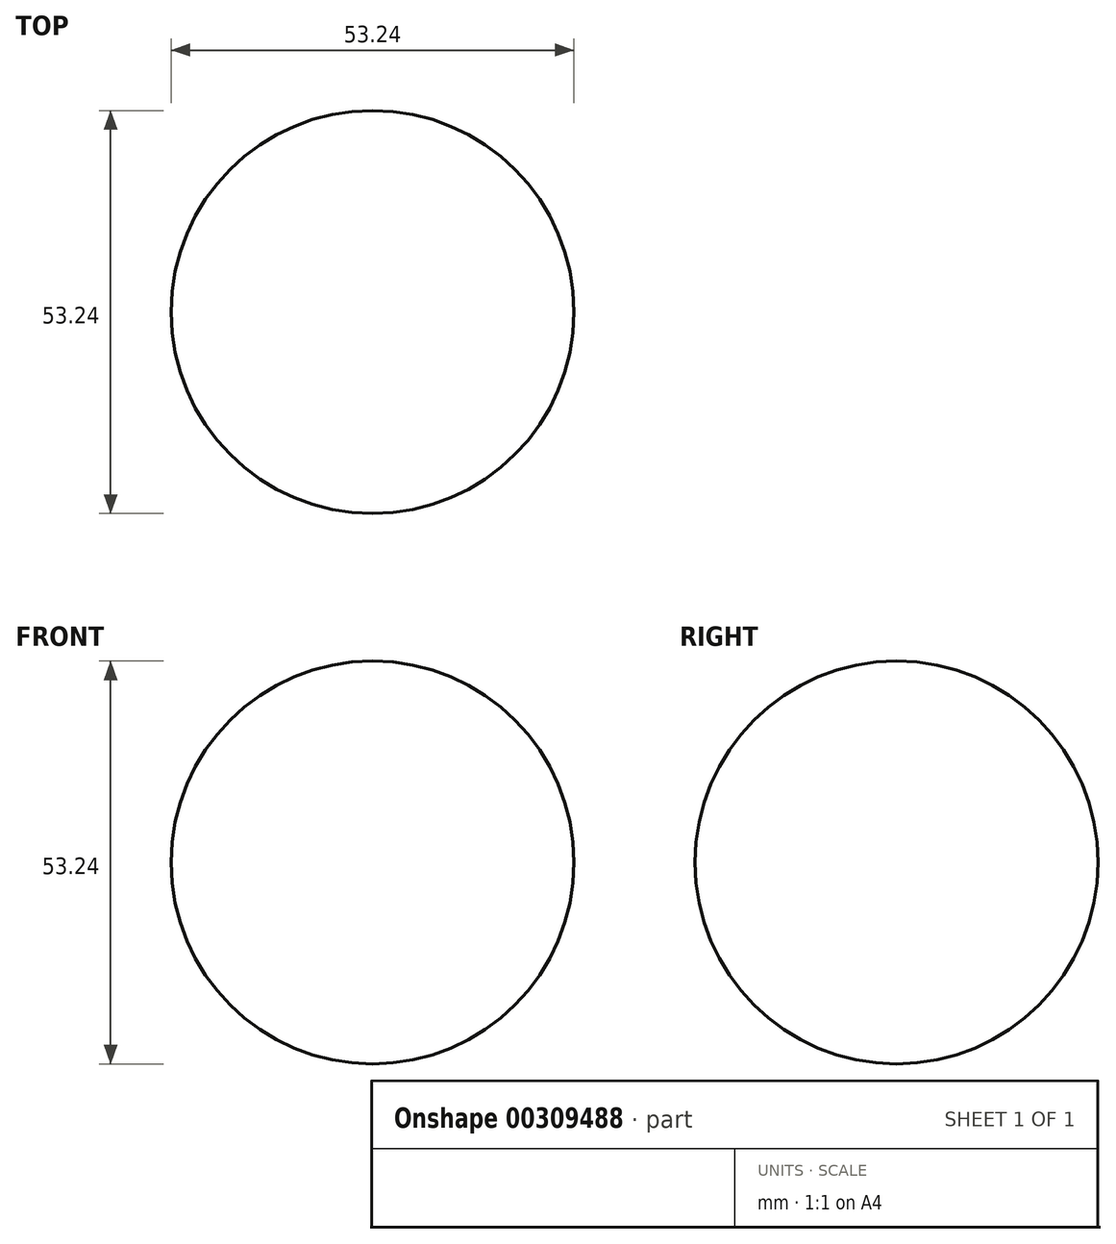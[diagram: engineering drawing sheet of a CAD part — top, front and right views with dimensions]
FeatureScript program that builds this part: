
annotation { "Feature Type Name" : "Feature", "Feature Type Description" : "" }
export const myFeature = defineFeature(function(context is Context, id is Id, definition is map)
    precondition{}
    {
        {
            var Q0;
            Q0=qCreatedBy(makeId("Front.planeOp"),FACE);
            var sketch = newSketch(context, id + "F0", { "sketchPlane" : qUnion([Q0])});
            skArc(sketch, "E0", {"start": v(0, 26.62) * mm, "mid": v(-26.62, 0) * mm, "end": v(0, -26.62) * mm});
            skLineSegment(sketch, "E1", {"start": v(0, 26.62) * mm, "end": v(0, -26.62) * mm, "construction": true});
            skSolve(sketch);
        }
        {
            var Q0;
            Q0=sQuery(id+"F0.wireOp",EDGE,"E0");
            var Q1;
            Q1=sQuery(id+"F0.wireOp",EDGE,"E1");
            revolve(context, id + "F1", {"bodyType" : ToolBodyType.SURFACE, "surfaceEntities" : qUnion([Q0]), "axis" : qUnion([Q1]), "revolveType" : RevolveType.FULL});
        }
    });
